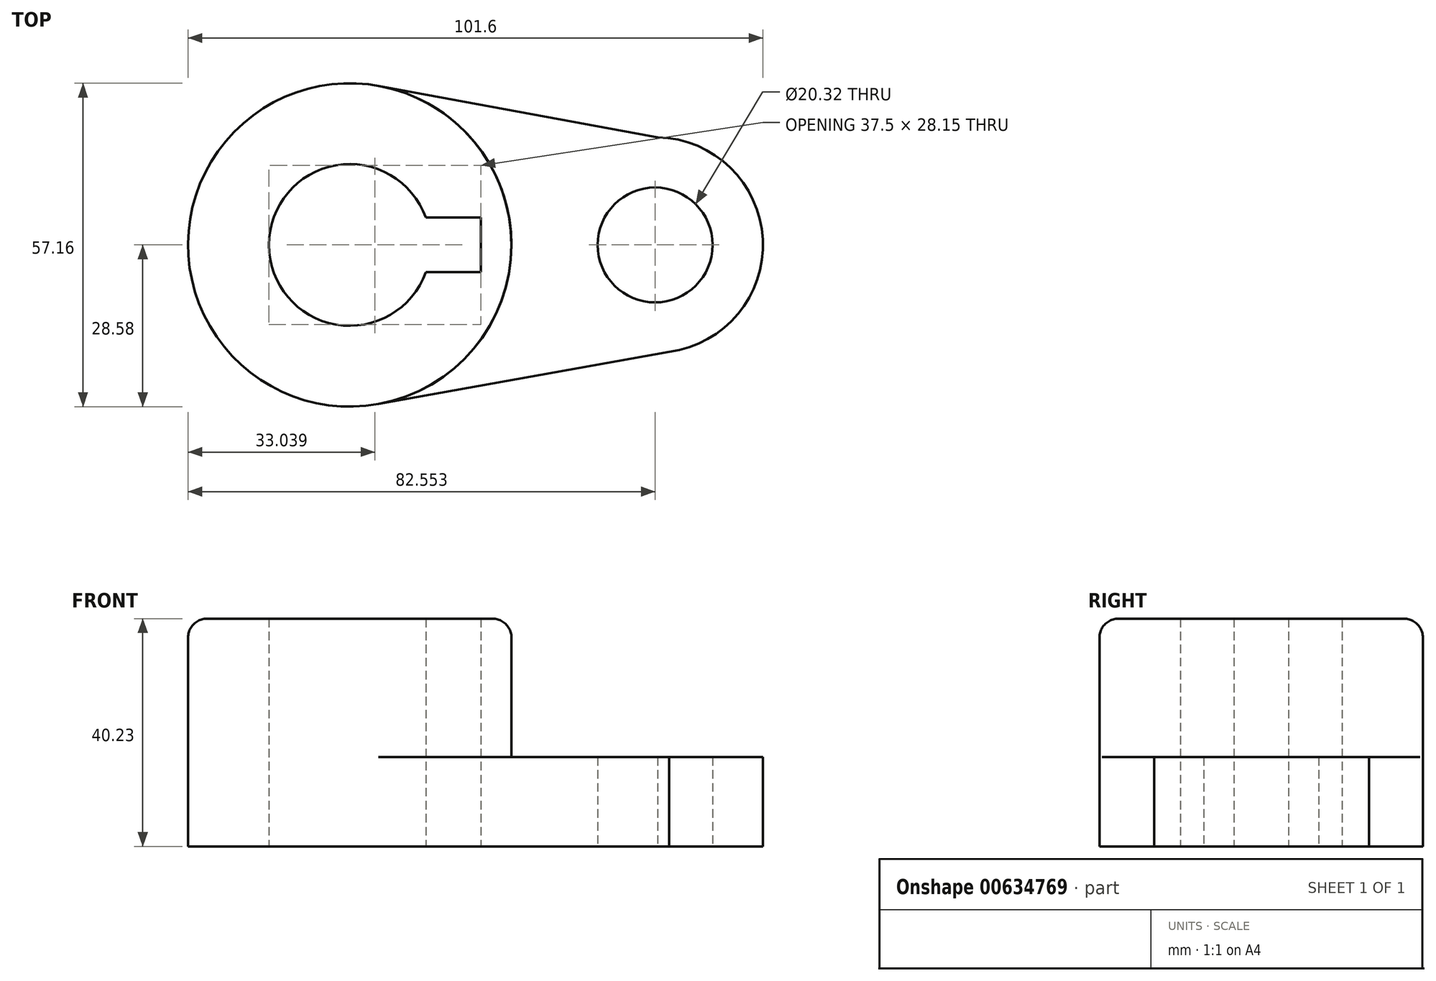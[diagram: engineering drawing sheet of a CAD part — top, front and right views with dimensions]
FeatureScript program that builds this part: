
annotation { "Feature Type Name" : "Feature", "Feature Type Description" : "" }
export const myFeature = defineFeature(function(context is Context, id is Id, definition is map)
    precondition{}
    {
        {
            var Q0;
            Q0=qCreatedBy(makeId("Top.planeOp"),FACE);
            var sketch = newSketch(context, id + "F0", { "sketchPlane" : qUnion([Q0])});
            skLineSegment(sketch, "E0", {"start": v(-35.27, 0) * mm, "end": v(18.7, 0) * mm});
            skCircle(sketch, "E1", {"center": v(-35.27, 0) * mm, "radius": 14.29 * mm});
            skCircle(sketch, "E2", {"center": v(18.7, 0) * mm, "radius": 19.05 * mm});
            skCircle(sketch, "E3", {"center": v(-35.27, 0) * mm, "radius": 28.58 * mm});
            skCircle(sketch, "E4", {"center": v(18.7, 0) * mm, "radius": 10.16 * mm});
            skLineSegment(sketch, "E5", {"start": v(-30.1, 28.1) * mm, "end": v(19.15, 19.04) * mm});
            skLineSegment(sketch, "E6", {"start": v(21.16, -18.9) * mm, "end": v(-30.22, -28.12) * mm});
            skLineSegment(sketch, "E7", {"start": v(-35.27, 0) * mm, "end": v(-12.06, 0) * mm});
            skLineSegment(sketch, "E8", {"start": v(-39.51, 0) * mm, "end": v(-6.7, 0) * mm});
            skLineSegment(sketch, "E9", {"start": v(-12.06, 0) * mm, "end": v(-12.06, -4.83) * mm});
            skLineSegment(sketch, "E10", {"start": v(-12.06, 0) * mm, "end": v(-12.06, 4.83) * mm});
            skLineSegment(sketch, "E11", {"start": v(-12.06, 4.83) * mm, "end": v(-21.82, 4.83) * mm});
            skLineSegment(sketch, "E12", {"start": v(-12.06, -4.83) * mm, "end": v(-21.82, -4.83) * mm});
            skSolve(sketch);
        }
        {
            var Q0;
            Q0=makeQuery(id+"F0.imprint","IMPRINT",FACE,{"disambiguationData":[TD([[makeQuery(id+"F0.imprint","IMPRINT",EDGE,{"derivedFrom":sQuery(id+"F0.wireOp",EDGE,"E9")}),1.0]])]});
            extrude(context, id + "F1", {"entities" : qUnion([Q0]), "depth" : 40.23 * mm, "offsetDistance" : 25.4 * mm});
        }
        {
            var Q0;
            {var subQ5=sQuery(id+"F0.wireOp",EDGE,"E6");Q0=makeQuery(id+"F0.imprint","IMPRINT",FACE,{"disambiguationData":[TD([[makeQuery(id+"F0.imprint","IMPRINT",EDGE,{"derivedFrom":subQ5}),-1.0]])]});}
            var Q1;
            {var subQ5=sQuery(id+"F0.wireOp",EDGE,"E5");Q1=makeQuery(id+"F0.imprint","IMPRINT",FACE,{"disambiguationData":[TD([[makeQuery(id+"F0.imprint","IMPRINT",EDGE,{"derivedFrom":subQ5}),-1.0]])]});}
            var Q2;
            Q2=makeQuery(id+"F0.imprint","IMPRINT",FACE,{"disambiguationData":[TD([[makeQuery(id+"F0.imprint","IMPRINT",EDGE,{"derivedFrom":sQuery(id+"F0.wireOp",EDGE,"E4")}),-1.0]])]});
            extrude(context, id + "F2", {"entities" : qUnion([Q0, Q1, Q2]), "operationType" : NewBodyOperationType.ADD, "depth" : 15.77 * mm, "offsetDistance" : 25.4 * mm});
        }
        {
            var Q0;
            Q0=makeQuery(id+"F1.opExtrude","CAP_EDGE",EDGE,{"disambiguationData":[OSD([sQuery(id+"F0.wireOp",EDGE,"E3")])],"isStart":false});
            fillet(context, id + "F3", {"entities" : qUnion([Q0]), "radius" : 3.3 * mm, "tangentPropagation" : true, "allowEdgeOverflow" : false});
        }
    });
